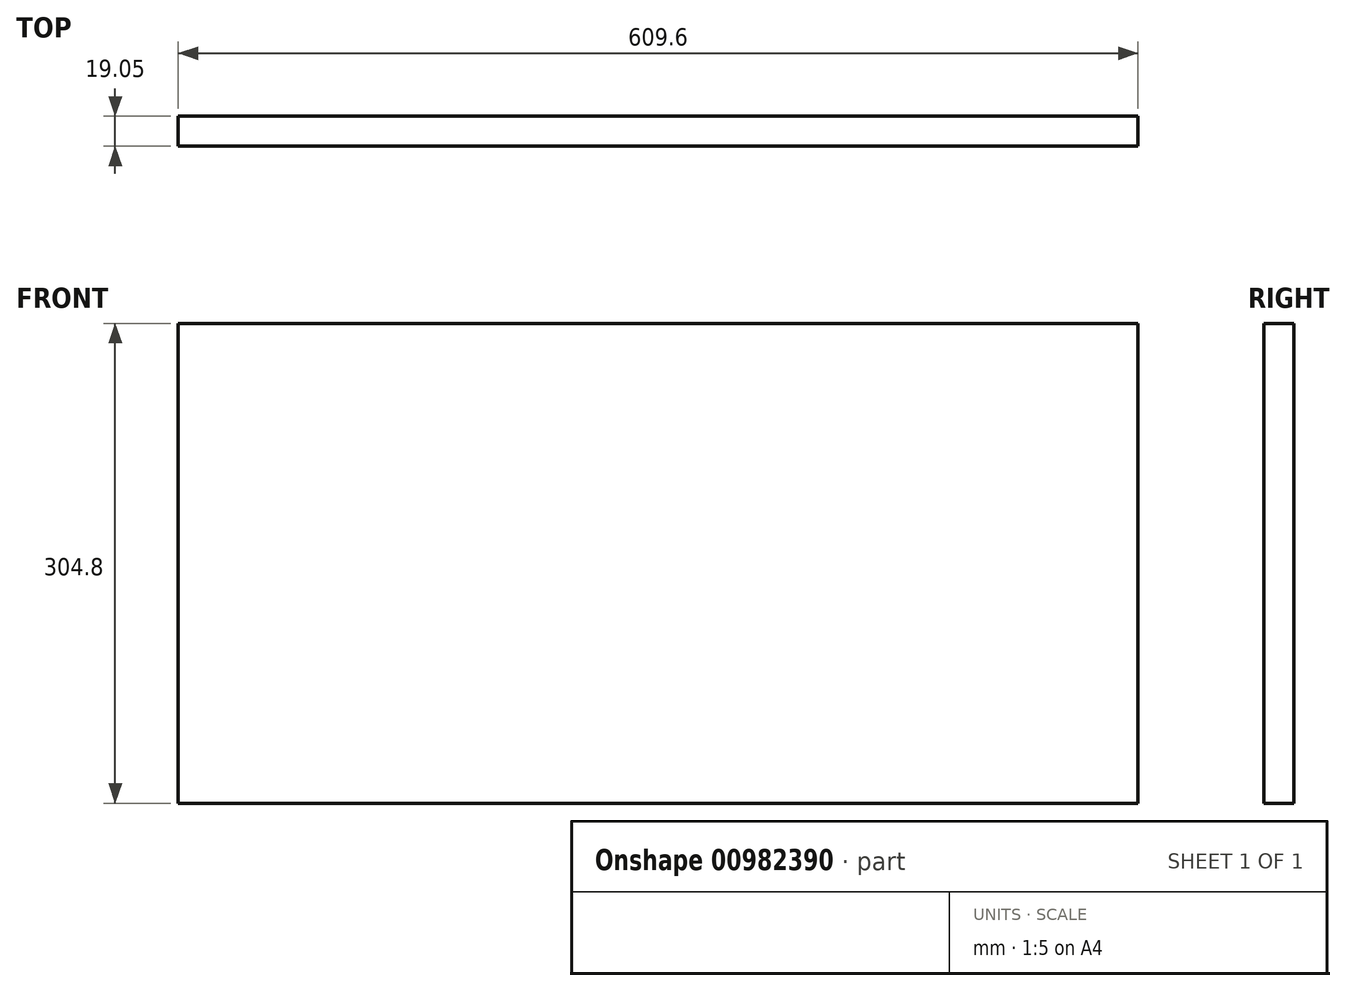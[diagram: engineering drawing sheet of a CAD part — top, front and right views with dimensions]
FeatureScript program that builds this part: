
annotation { "Feature Type Name" : "Feature", "Feature Type Description" : "" }
export const myFeature = defineFeature(function(context is Context, id is Id, definition is map)
    precondition{}
    {
        {
            var Q0;
            Q0=qCreatedBy(makeId("Front.planeOp"),FACE);
            var sketch = newSketch(context, id + "F0", { "sketchPlane" : qUnion([Q0])});
            skLineSegment(sketch, "E0.bottom", {"start": v(503.5, -14.29) * mm, "end": v(-106.1, -14.29) * mm});
            skLineSegment(sketch, "E0.top", {"start": v(503.5, 290.51) * mm, "end": v(-106.1, 290.51) * mm});
            skLineSegment(sketch, "E0.left", {"start": v(503.5, -14.29) * mm, "end": v(503.5, 290.51) * mm});
            skLineSegment(sketch, "E0.right", {"start": v(-106.1, -14.29) * mm, "end": v(-106.1, 290.51) * mm});
            skPoint(sketch, "E0.middle", {"position": v(198.7, 138.11) * mm});
            skSolve(sketch);
        }
        {
            var Q0;
            Q0=makeQuery(id+"F0.imprint","IMPRINT",FACE,{"disambiguationData":[TD([[makeQuery(id+"F0.imprint","IMPRINT",EDGE,{"derivedFrom":sQuery(id+"F0.wireOp",EDGE,"E0.bottom")}),-1.0]])]});
            extrude(context, id + "F1", {"entities" : qUnion([Q0]), "depth" : 19.05 * mm, "offsetDistance" : 25.4 * mm});
        }
    });
